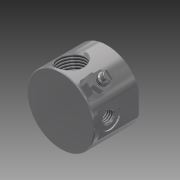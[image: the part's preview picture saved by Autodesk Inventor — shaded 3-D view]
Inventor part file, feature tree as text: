
AUTODESK INVENTOR PART (.ipt)
format: ipt  version: 2016 SP1 (Build 200210100, 210)  size: 280,064 bytes
history: native  units: in
note: dims shown in document units (in); Inventor stores cm internally (conversion verified against a paired STEP export)
features: other x35, sketch x14, revolve x5, extrude x5, hole x4, thread x4
ambient origin geometry x8: Origin, YZ Plane, XZ Plane, XY Plane, X Axis, Y Axis, Z Axis, Center Point
bodies: Solid1 (feature_tree)
feature tree (67):
  revolve  "Revolution1"  [1 undecoded]
  hole  "Hole1"  [1 undecoded]
  hole  "Hole2"  [1 undecoded]
  hole  "Hole3"  [1 undecoded]
  hole  "Hole4"  [1 undecoded]
  extrude  "Extrusion1"  Depth=0.252in TaperAngle=0.0deg
  revolve  "Revolution2"  [1 undecoded]
  thread  "Thread1"  [1 undecoded]
  revolve  "Revolution3"  [1 undecoded]
  thread  "Thread2"  [1 undecoded]
  extrude  "Extrusion2"  [1 undecoded]
  extrude  "Extrusion3"  [1 undecoded]
  extrude  "Extrusion4"  [1 undecoded]
  revolve  "Revolution4"  [1 undecoded]
  thread  "Thread3"  [1 undecoded]
  extrude  "Extrusion5"  [1 undecoded]
  revolve  "Revolution5"  [1 undecoded]
  thread  "Thread4"  [1 undecoded]
  other  "conn_XY"
  other  "conn_YZ"
  other  "conn_ZX"
  other  "conn_X"
  other  "conn_Y"
  other  "conn_Z"
  other  "conn_Center"
  other  "conn2_XY"
  other  "conn2_YZ"
  other  "conn2_ZX"
  other  "conn2_X"
  other  "conn2_Y"
  other  "conn2_Z"
  other  "conn2_Center"
  other  "mnt_XY"
  other  "mnt_YZ"
  other  "mnt_ZX"
  other  "mnt_X"
  other  "mnt_Y"
  other  "mnt_Z"
  other  "mnt_Center"
  other  "trun1_XY"
  other  "trun1_YZ"
  other  "trun1_ZX"
  other  "trun1_X"
  other  "trun1_Y"
  other  "trun1_Z"
  other  "trun1_Center"
  other  "trun2_XY"
  other  "trun2_YZ"
  other  "trun2_ZX"
  other  "trun2_X"
  other  "trun2_Y"
  other  "trun2_Z"
  other  "trun2_Center"
  sketch  "Sketch_3"  dims[d1=0.134in d2=0.28in d3=0.164in d4=0.25in d5=90.0deg d6=0.28in d7=0.8383in]
  sketch  "Sketch2"  dims[d0=360.0deg]
  sketch  "Sketch3"  dims[d8=0.134in d9=0.28in d10=0.164in d11=0.25in d12=90.0deg d13=0.28in d14=0.8383in]
  sketch  "Sketch4"  dims[d15=0.134in d16=0.28in d17=0.164in d18=0.25in d19=90.0deg d20=0.28in d21=0.8383in]
  sketch  "Sketch5"  dims[d22=0.134in d23=0.28in d24=0.164in d25=0.25in d26=90.0deg d27=0.28in d28=0.8383in d29=0.63in d30=0.0in]
  sketch  "Sketch_6"  dims[d31=360.0deg d32=0.1399in d33=0.0in]
  sketch  "Sketch_7"  dims[d34=360.0deg d35=0.1399in d36=0.0in]
  sketch  "Sketch_8"  dims[d37=0.138in d38=0.0in d39=0.138in d40=0.0in]
  sketch  "Sketch_13"
  sketch  "Sketch_14"
  sketch  "Sketch_15"
  sketch  "Sketch_9"  dims[d41=0.094in d42=0.0in d43=360.0deg]
  sketch  "Sketch_11"  dims[d48=360.0deg d49=0.2731in d50=0.0in d51=0.0in d52=0.0in d53=0.0in d54=0.0in]
  sketch  "Sketch_10"  dims[d44=0.0573in d45=0.0in d46=0.252in d47=0.0in]
note: 17 required parameter values undecoded (feature->parameter linkage not recoverable at this tier; creation-order binding heuristic only, values carry confidence <= 0.55)